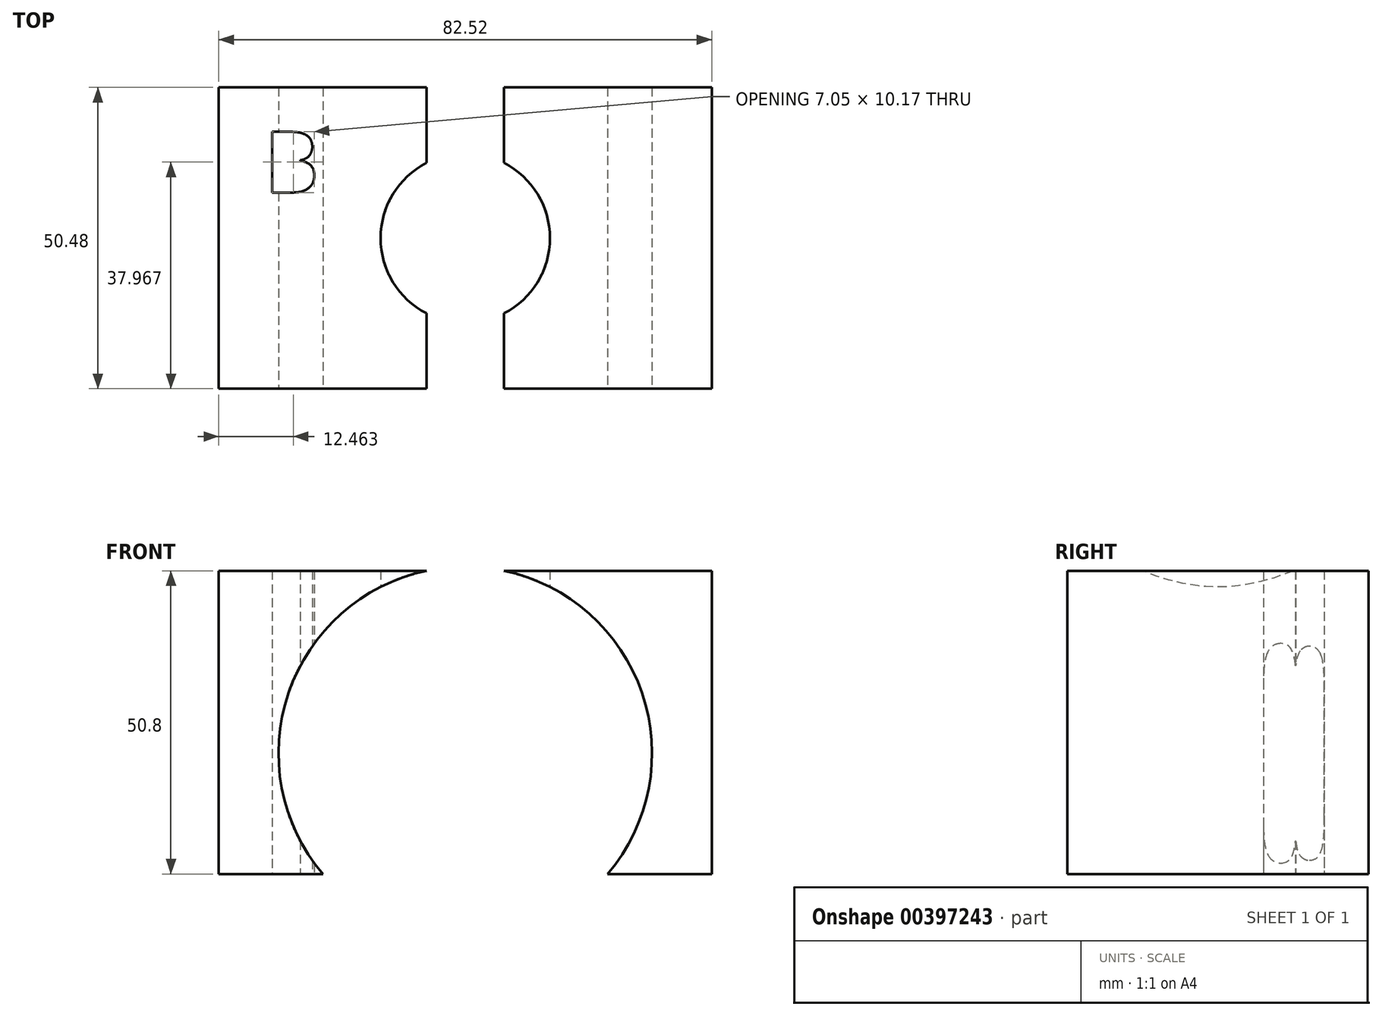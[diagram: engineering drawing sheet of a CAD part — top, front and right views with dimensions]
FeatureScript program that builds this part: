
annotation { "Feature Type Name" : "Feature", "Feature Type Description" : "" }
export const myFeature = defineFeature(function(context is Context, id is Id, definition is map)
    precondition{}
    {
        {
            var Q0;
            Q0=qCreatedBy(makeId("Top.planeOp"),FACE);
            var sketch = newSketch(context, id + "F0", { "sketchPlane" : qUnion([Q0])});
            skLineSegment(sketch, "E0.bottom", {"start": v(41.26, 25.24) * mm, "end": v(-41.26, 25.24) * mm});
            skLineSegment(sketch, "E0.top", {"start": v(41.26, -25.24) * mm, "end": v(-41.26, -25.24) * mm});
            skLineSegment(sketch, "E0.left", {"start": v(41.26, 25.24) * mm, "end": v(41.26, -25.24) * mm});
            skLineSegment(sketch, "E0.right", {"start": v(-41.26, 25.24) * mm, "end": v(-41.26, -25.24) * mm});
            skPoint(sketch, "E0.middle", {"position": v(0, 0) * mm});
            skCircle(sketch, "E1", {"center": v(0, 0) * mm, "radius": 14.18 * mm});
            skText(sketch, "E2", { "text": "B\n", "fontName": "OpenSans-Regular.ttf"});
            const initialGuessF0  = {"E2": [-0.03372, 0.00764, 1, 0, 0.01026]};
            skSetInitialGuess(sketch, initialGuessF0);
            skSolve(sketch);
        }
        {
            var Q0;
            Q0 = qSketchRegion(id + "F0", true);
            extrude(context, id + "F1", {"entities" : qUnion([Q0]), "depth" : 25.4 * mm, "offsetDistance" : 25.4 * mm});
        }
        {
            var Q0;
            Q0=makeQuery(id+"F1.opExtrude","CAP_FACE",FACE,{"disambiguationData":[OSD([sQuery(id+"F0.wireOp",EDGE,"E0.bottom"),sQuery(id+"F0.wireOp",EDGE,"E0.top"),sQuery(id+"F0.wireOp",EDGE,"E0.left"),sQuery(id+"F0.wireOp",EDGE,"E0.right"),sQuery(id+"F0.wireOp",EDGE,"E1"),sQuery(id+"F0.wireOp",EDGE,"E2.sketch_text.stroke-0"),sQuery(id+"F0.wireOp",EDGE,"E2.sketch_text.stroke-1"),sQuery(id+"F0.wireOp",EDGE,"E2.sketch_text.stroke-2"),sQuery(id+"F0.wireOp",EDGE,"E2.sketch_text.stroke-3"),sQuery(id+"F0.wireOp",EDGE,"E2.sketch_text.stroke-4"),sQuery(id+"F0.wireOp",EDGE,"E2.sketch_text.stroke-5"),sQuery(id+"F0.wireOp",EDGE,"E2.sketch_text.stroke-6"),sQuery(id+"F0.wireOp",EDGE,"E2.sketch_text.stroke-7"),sQuery(id+"F0.wireOp",EDGE,"E2.sketch_text.stroke-8"),sQuery(id+"F0.wireOp",EDGE,"E2.sketch_text.stroke-9"),sQuery(id+"F0.wireOp",EDGE,"E2.sketch_text.stroke-10")])],"isStart":false});
            var sketch = newSketch(context, id + "F2", { "sketchPlane" : qUnion([Q0])});
            skSolve(sketch);
        }
        {
            var Q0;
            Q0=makeQuery(id+"F2.imprint","IMPRINT",FACE,{"disambiguationData":[TD([[makeQuery(id+"F2.imprint","IMPRINT",EDGE,{"derivedFrom":makeQuery(id+"F1.opExtrude","CAP_EDGE",EDGE,{"disambiguationData":[OSD([sQuery(id+"F0.wireOp",EDGE,"E0.bottom")])],"isStart":false})}),1.0]])]});
            extrude(context, id + "F3", {"entities" : qUnion([Q0]), "operationType" : NewBodyOperationType.ADD, "depth" : 25.4 * mm, "offsetDistance" : 25.4 * mm});
        }
        {
            var Q0;
            {var subQ0=sQuery(id+"F0.wireOp",EDGE,"E0.top");Q0=makeQuery(id+"F3.boolean.opBoolean","MERGE",FACE,{"derivedFrom":[makeQuery(id+"F1.opExtrude","SWEPT_FACE",FACE,{"disambiguationData":[OSD([subQ0])]}),makeQuery(id+"F3.opExtrude","SWEPT_FACE",FACE,{"disambiguationData":[OSD([subQ0])]})]});}
            var sketch = newSketch(context, id + "F4", { "sketchPlane" : qUnion([Q0])});
            skCircle(sketch, "E3", {"center": v(0, 20.22) * mm, "radius": 31.26 * mm});
            skSolve(sketch);
        }
        {
            var Q0;
            {var subQ0=sQuery(id+"F4.wireOp",EDGE,"E3");var subQ1=makeQuery(id+"F3.opExtrude","CAP_EDGE",EDGE,{"disambiguationData":[OSD([sQuery(id+"F0.wireOp",EDGE,"E0.top")])],"isStart":false});var subQ2=makeQuery(id+"F4.imprint","INTERSECT",VERTEX,{"disambiguationData":[OD(0.0)],"derivedFrom":[subQ1,subQ0]});Q0=makeQuery(id+"F4.imprint","IMPRINT",FACE,{"disambiguationData":[TD([[makeQuery(id+"F4.imprint","IMPRINT",EDGE,{"disambiguationData":[TD([[subQ2,-1.0]])],"derivedFrom":subQ0}),1.0]])]});}
            var Q1;
            {var subQ0=sQuery(id+"F4.wireOp",EDGE,"E3");var subQ1=makeQuery(id+"F3.opExtrude","CAP_EDGE",EDGE,{"disambiguationData":[OSD([sQuery(id+"F0.wireOp",EDGE,"E0.top")])],"isStart":false});var subQ2=makeQuery(id+"F4.imprint","INTERSECT",VERTEX,{"disambiguationData":[OD(0.0)],"derivedFrom":[subQ1,subQ0]});Q1=makeQuery(id+"F4.imprint","IMPRINT",FACE,{"disambiguationData":[TD([[makeQuery(id+"F4.imprint","IMPRINT",EDGE,{"disambiguationData":[TD([[subQ2,1.0]])],"derivedFrom":subQ0}),1.0]])]});}
            extrude(context, id + "F5", {"entities" : qUnion([Q0, Q1]), "operationType" : NewBodyOperationType.REMOVE, "oppositeDirection" : true, "depth" : 68.07 * mm, "offsetDistance" : 25.4 * mm});
        }
    });
